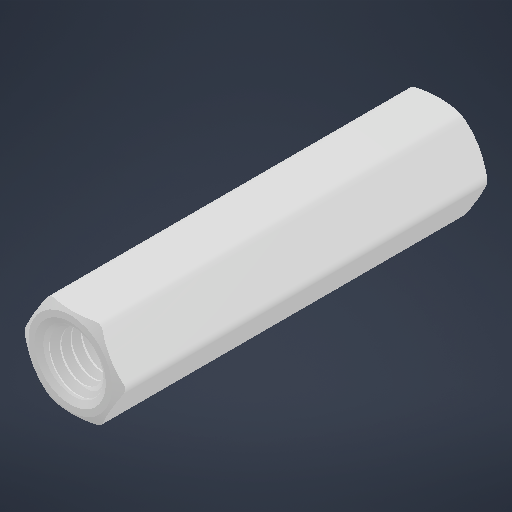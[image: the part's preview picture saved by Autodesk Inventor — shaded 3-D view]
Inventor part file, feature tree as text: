
AUTODESK INVENTOR PART (.ipt)
format: ipt  version: 2025.2 (Build 292293000, 293)  size: 658,432 bytes
history: native  units: in
note: dims shown in document units (in); Inventor stores cm internally (conversion verified against a paired STEP export)
features: other x1, mirror x1
ambient origin geometry x8: Origin, YZ Plane, XZ Plane, XY Plane, X Axis, Y Axis, Z Axis, Center Point
bodies: Solid1 (feature_tree)
feature tree (2):
  other  "Plane1"
  mirror  "Mirror1"
